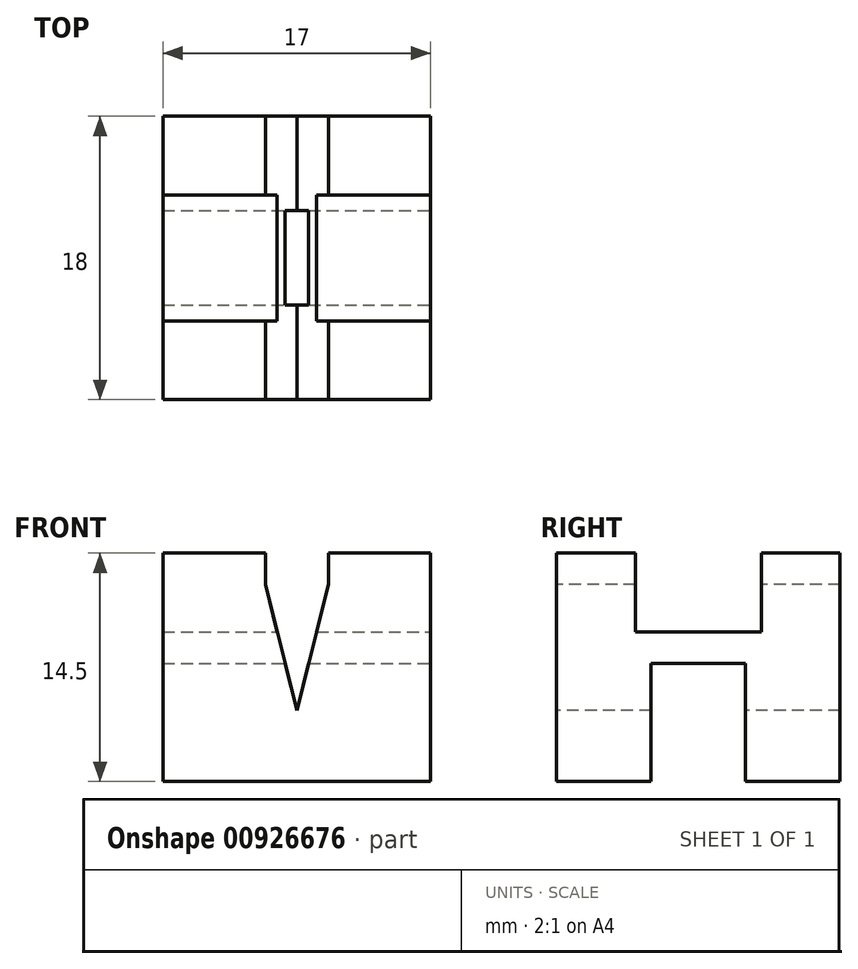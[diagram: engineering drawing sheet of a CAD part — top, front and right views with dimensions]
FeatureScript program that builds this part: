
annotation { "Feature Type Name" : "Feature", "Feature Type Description" : "" }
export const myFeature = defineFeature(function(context is Context, id is Id, definition is map)
    precondition{}
    {
        {
            var Q0;
            Q0=qCreatedBy(makeId("Front.planeOp"),FACE);
            var sketch = newSketch(context, id + "F0", { "sketchPlane" : qUnion([Q0])});
            skLineSegment(sketch, "E0.bottom", {"start": v(0, 0) * mm, "end": v(17, 0) * mm});
            skLineSegment(sketch, "E0.top", {"start": v(0, 11) * mm, "end": v(17, 11) * mm});
            skLineSegment(sketch, "E0.left", {"start": v(0, 0) * mm, "end": v(0, 11) * mm});
            skLineSegment(sketch, "E0.right", {"start": v(17, 0) * mm, "end": v(17, 11) * mm});
            skSolve(sketch);
        }
        {
            var Q0;
            Q0 = qSketchRegion(id + "F0", true);
            extrude(context, id + "F1", {"entities" : qUnion([Q0]), "depth" : 18 * mm, "offsetDistance" : 25 * mm});
        }
        {
            var Q0;
            Q0=makeQuery(id+"F1.opExtrude","CAP_FACE",FACE,{"disambiguationData":[OSD([sQuery(id+"F0.wireOp",EDGE,"E0.bottom"),sQuery(id+"F0.wireOp",EDGE,"E0.top"),sQuery(id+"F0.wireOp",EDGE,"E0.left"),sQuery(id+"F0.wireOp",EDGE,"E0.right")])],"isStart":false});
            var sketch = newSketch(context, id + "F2", { "sketchPlane" : qUnion([Q0])});
            skLineSegment(sketch, "E1", {"start": v(17, 11) * mm, "end": v(10.5, 11) * mm});
            skLineSegment(sketch, "E2", {"start": v(0, 11) * mm, "end": v(6.5, 11) * mm});
            skLineSegment(sketch, "E3", {"start": v(6.5, 11) * mm, "end": v(6.5, 9) * mm});
            skLineSegment(sketch, "E4", {"start": v(10.5, 11) * mm, "end": v(10.5, 9) * mm});
            skLineSegment(sketch, "E5", {"start": v(6.5, 9) * mm, "end": v(8.5, 1) * mm});
            skLineSegment(sketch, "E6", {"start": v(10.5, 9) * mm, "end": v(8.5, 1) * mm});
            skSolve(sketch);
        }
        {
            var Q0;
            {var subQ1=sQuery(id+"F2.wireOp",EDGE,"E3");Q0=makeQuery(id+"F2.imprint","IMPRINT",FACE,{"disambiguationData":[TD([[makeQuery(id+"F2.imprint","IMPRINT",EDGE,{"derivedFrom":subQ1}),1.0]])]});}
            extrude(context, id + "F3", {"entities" : qUnion([Q0]), "operationType" : NewBodyOperationType.REMOVE, "oppositeDirection" : true, "depth" : 25 * mm, "offsetDistance" : 25 * mm});
        }
        {
            var Q0;
            Q0=makeQuery(id+"F1.opExtrude","SWEPT_FACE",FACE,{"disambiguationData":[OSD([sQuery(id+"F0.wireOp",EDGE,"E0.right")])]});
            var sketch = newSketch(context, id + "F4", { "sketchPlane" : qUnion([Q0])});
            skLineSegment(sketch, "E7", {"start": v(-18, 11) * mm, "end": v(-13, 11) * mm});
            skLineSegment(sketch, "E8.bottom", {"start": v(-13, 11) * mm, "end": v(-5, 11) * mm});
            skLineSegment(sketch, "E8.top", {"start": v(-13, 6) * mm, "end": v(-5, 6) * mm});
            skLineSegment(sketch, "E8.left", {"start": v(-13, 11) * mm, "end": v(-13, 6) * mm});
            skLineSegment(sketch, "E8.right", {"start": v(-5, 11) * mm, "end": v(-5, 6) * mm});
            skSolve(sketch);
        }
        {
            var Q0;
            Q0=makeQuery(id+"F4.imprint","IMPRINT",FACE,{"disambiguationData":[TD([[makeQuery(id+"F4.imprint","IMPRINT",EDGE,{"derivedFrom":sQuery(id+"F4.wireOp",EDGE,"E8.bottom")}),-1.0]])]});
            extrude(context, id + "F5", {"entities" : qUnion([Q0]), "operationType" : NewBodyOperationType.REMOVE, "oppositeDirection" : true, "depth" : 25 * mm, "offsetDistance" : 25 * mm});
        }
        {
            var Q0;
            Q0=makeQuery(id+"F1.opExtrude","SWEPT_FACE",FACE,{"disambiguationData":[OSD([sQuery(id+"F0.wireOp",EDGE,"E0.right")])]});
            var sketch = newSketch(context, id + "F6", { "sketchPlane" : qUnion([Q0])});
            skLineSegment(sketch, "E9", {"start": v(-9, 6) * mm, "end": v(-9, 4) * mm});
            skLineSegment(sketch, "E10", {"start": v(-9, 4) * mm, "end": v(-6, 4) * mm});
            skLineSegment(sketch, "E11", {"start": v(-9, 4) * mm, "end": v(-12, 4) * mm});
            skLineSegment(sketch, "E12", {"start": v(-12, 4) * mm, "end": v(-12, 0) * mm});
            skLineSegment(sketch, "E13", {"start": v(-6, 4) * mm, "end": v(-6, 0) * mm});
            skSolve(sketch);
        }
        {
            var Q0;
            Q0=makeQuery(id+"F6.imprint","IMPRINT",FACE,{"disambiguationData":[TD([[makeQuery(id+"F6.imprint","IMPRINT",EDGE,{"derivedFrom":sQuery(id+"F6.wireOp",EDGE,"E10")}),-1.0]])]});
            extrude(context, id + "F7", {"entities" : qUnion([Q0]), "operationType" : NewBodyOperationType.REMOVE, "oppositeDirection" : true, "depth" : 25 * mm, "offsetDistance" : 25 * mm});
        }
        {
            var Q0;
            Q0=makeQuery(id+"F1.opExtrude","SWEPT_FACE",FACE,{"disambiguationData":[OSD([sQuery(id+"F0.wireOp",EDGE,"E0.right")])]});
            var sketch = newSketch(context, id + "F8", { "sketchPlane" : qUnion([Q0])});
            skLineSegment(sketch, "E14.bottom", {"start": v(-6, 0) * mm, "end": v(0, 0) * mm});
            skLineSegment(sketch, "E15.top", {"start": v(-6, -3.5) * mm, "end": v(0, -3.5) * mm});
            skLineSegment(sketch, "E15.left", {"start": v(-6, 0) * mm, "end": v(-6, -3.5) * mm});
            skLineSegment(sketch, "E15.right", {"start": v(0, 0) * mm, "end": v(0, -3.5) * mm});
            skSolve(sketch);
        }
        {
            var Q0;
            Q0=makeQuery(id+"F8.imprint","IMPRINT",FACE,{"disambiguationData":[TD([[makeQuery(id+"F8.imprint","IMPRINT",EDGE,{"derivedFrom":sQuery(id+"F8.wireOp",EDGE,"E14.bottom")}),-1.0]])]});
            extrude(context, id + "F9", {"entities" : qUnion([Q0]), "operationType" : NewBodyOperationType.ADD, "depth" : -17 * mm, "offsetDistance" : 25 * mm});
        }
        {
            var Q0;
            Q0=makeQuery(id+"F9.boolean.opBoolean","MERGE",FACE,{"derivedFrom":[makeQuery(id+"F1.opExtrude","SWEPT_FACE",FACE,{"disambiguationData":[OSD([sQuery(id+"F0.wireOp",EDGE,"E0.right")])]}),makeQuery(id+"F9.opExtrude","CAP_FACE",FACE,{"disambiguationData":[OSD([sQuery(id+"F8.wireOp",EDGE,"E14.bottom"),sQuery(id+"F8.wireOp",EDGE,"E15.top"),sQuery(id+"F8.wireOp",EDGE,"E15.left"),sQuery(id+"F8.wireOp",EDGE,"E15.right")])],"isStart":true})]});
            var sketch = newSketch(context, id + "F10", { "sketchPlane" : qUnion([Q0])});
            skLineSegment(sketch, "E16.bottom", {"start": v(-18, 0) * mm, "end": v(-12, 0) * mm});
            skLineSegment(sketch, "E16.top", {"start": v(-18, -3.5) * mm, "end": v(-12, -3.5) * mm});
            skLineSegment(sketch, "E16.left", {"start": v(-18, 0) * mm, "end": v(-18, -3.5) * mm});
            skLineSegment(sketch, "E16.right", {"start": v(-12, 0) * mm, "end": v(-12, -3.5) * mm});
            skSolve(sketch);
        }
        {
            var Q0;
            Q0=makeQuery(id+"F10.imprint","IMPRINT",FACE,{"disambiguationData":[TD([[makeQuery(id+"F10.imprint","IMPRINT",EDGE,{"derivedFrom":sQuery(id+"F10.wireOp",EDGE,"E16.bottom")}),-1.0]])]});
            extrude(context, id + "F11", {"entities" : qUnion([Q0]), "operationType" : NewBodyOperationType.ADD, "depth" : -17 * mm, "offsetDistance" : 25 * mm});
        }
    });
